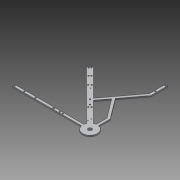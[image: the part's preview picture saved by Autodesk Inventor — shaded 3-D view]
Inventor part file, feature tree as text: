
AUTODESK INVENTOR PART (.ipt)
format: ipt  version: 2014 SP1 (Build 180222100, 222)  size: 231,936 bytes
history: native  units: in
note: dims shown in document units (in); Inventor stores cm internally (conversion verified against a paired STEP export)
features: reference x7, extrude x5, sketch x5, projected_geometry x1
ambient origin geometry x8: Origin, YZ Plane, XZ Plane, XY Plane, X Axis, Y Axis, Z Axis, Center Point
bodies: Solid1 (feature_tree)
feature tree (18):
  extrude  "Extrusion1"  Depth=0.25in TaperAngle=0.0deg
  extrude  "Extrusion6"  Depth=0.25in TaperAngle=0.0deg
  extrude  "Extrusion7"  TaperAngle=0.0deg  [1 undecoded]
  extrude  "Extrusion8"  Depth=1.0in TaperAngle=0.0deg
  extrude  "Extrusion9"  Depth=0.25in TaperAngle=0.0deg
  sketch  "Sketch1"  dims[d2=0.5in d3=0.5in d4=1.5in d6=1.5in d7=0.25in d8=0.25in d9=0.25in d10=0.5in d11=0.5in d12=3.75in d13=0.266in d14=0.266in d15=0.266in d16=0.25in d17=0.266in d18=0.25in d19=0.25in d20=0.266in d21=0.266in d22=0.266in d23=0.25in d24=0.266in d25=1.125in d28=1.5in d30=0.25in d31=5.5in d34=0.25in d37=10.926in d38=10.6389in d39=0.2871in d40=0.2871in d41=15.5in d42=15.5in d43=0.25in d44=0.5in d45=0.266in d46=0.25in d47=0.266in d48=0.266in d49=15.5in d50=0.25in d51=0.266in d52=0.25in d54=0.266in d55=0.266in d56=0.266in d57=2.0in d58=2.0in d59=2.0in d60=0.297in d61=0.297in d62=0.297in d63=0.297in d64=2.0in d67=0.25in d68=0.0in]
  sketch  "Sketch7"  dims[d99=0.748in d100=0.25in d101=0.0in]
  sketch  "Sketch9"  dims[d102=0.0in d103=0.0in]
  reference  "Reference6"
  sketch  "Sketch10"  dims[d104=0.0in d105=1.0in d106=0.0in]
  projected_geometry  "Projected Loop2"
  sketch  "Sketch11"  dims[d107=0.5in d109=0.25in d110=0.0in d111=1.0in d112=0.0in]
  reference  "Reference7"
  reference  "Reference8"
  reference  "Reference9"
  reference  "Reference10"
  reference  "Reference11"
  reference  "Reference12"
note: 1 required parameter value undecoded (feature->parameter linkage not recoverable at this tier; creation-order binding heuristic only, values carry confidence <= 0.55)
